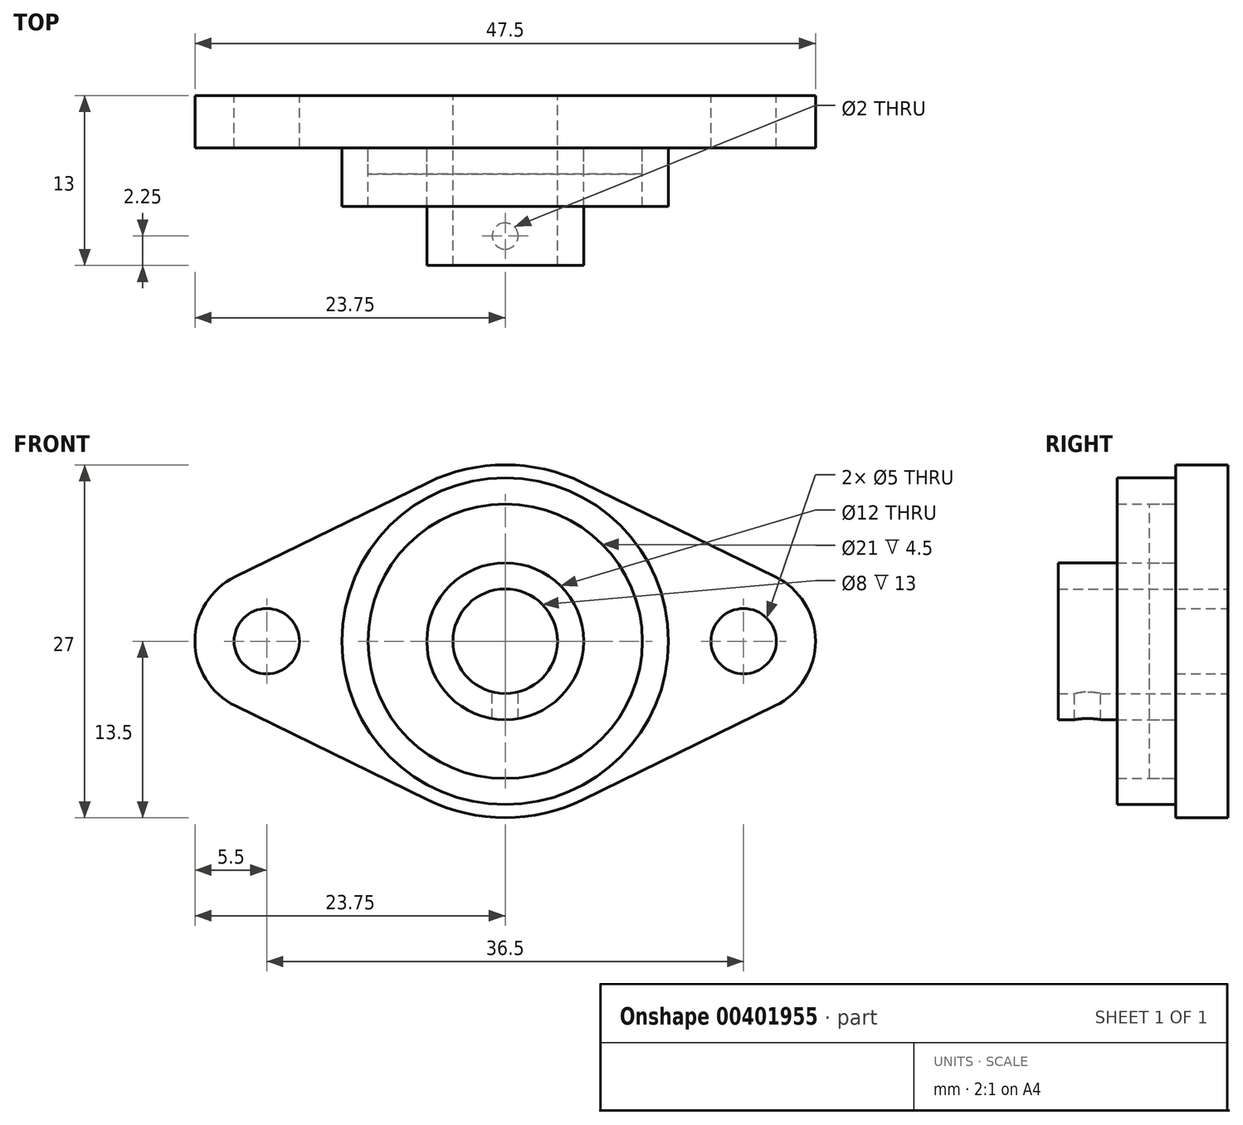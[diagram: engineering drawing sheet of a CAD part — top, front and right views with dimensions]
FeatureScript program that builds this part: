
annotation { "Feature Type Name" : "Feature", "Feature Type Description" : "" }
export const myFeature = defineFeature(function(context is Context, id is Id, definition is map)
    precondition{}
    {
        {
            var Q0;
            Q0=qCreatedBy(makeId("Front.planeOp"),FACE);
            var sketch = newSketch(context, id + "F0", { "sketchPlane" : qUnion([Q0])});
            skArc(sketch, "E0", {"start": v(-20.66, 4.94) * mm, "mid": v(-23.75, 0) * mm, "end": v(-20.66, -4.94) * mm});
            skArc(sketch, "E1", {"start": v(20.66, -4.94) * mm, "mid": v(23.75, 0) * mm, "end": v(20.66, 4.94) * mm});
            skLineSegment(sketch, "E2", {"start": v(-18.25, 0) * mm, "end": v(18.25, 0) * mm, "construction": true});
            skLineSegment(sketch, "E3", {"start": v(-20.66, 4.94) * mm, "end": v(-5.92, 12.13) * mm});
            skLineSegment(sketch, "E4", {"start": v(0, 0) * mm, "end": v(0, 24.56) * mm, "construction": true});
            skLineSegment(sketch, "E5.MirrorCS", {"start": v(20.66, 4.94) * mm, "end": v(5.92, 12.13) * mm});
            skLineSegment(sketch, "E6.MirrorCS", {"start": v(-20.66, -4.94) * mm, "end": v(-5.92, -12.13) * mm});
            skLineSegment(sketch, "E7.MirrorCS", {"start": v(20.66, -4.94) * mm, "end": v(5.92, -12.13) * mm});
            skArc(sketch, "E8.trimOffspring", {"start": v(5.92, 12.13) * mm, "mid": v(0, 13.5) * mm, "end": v(-5.92, 12.13) * mm});
            skArc(sketch, "E9.trimOffspring", {"start": v(-5.92, -12.13) * mm, "mid": v(0, -13.5) * mm, "end": v(5.92, -12.13) * mm});
            skCircle(sketch, "E10", {"center": v(-18.25, 0) * mm, "radius": 2.5 * mm});
            skCircle(sketch, "E11", {"center": v(18.25, 0) * mm, "radius": 2.5 * mm});
            skSolve(sketch);
        }
        {
            var Q0;
            Q0 = qSketchRegion(id + "F0", true);
            extrude(context, id + "F1", {"entities" : qUnion([Q0]), "endBound" : BoundingType.SYMMETRIC, "depth" : 4 * mm});
        }
        {
            var Q0;
            Q0=makeQuery(id+"F1.opExtrude","CAP_FACE",FACE,{"disambiguationData":[OSD([sQuery(id+"F0.wireOp",EDGE,"E0"),sQuery(id+"F0.wireOp",EDGE,"E1"),sQuery(id+"F0.wireOp",EDGE,"E3"),sQuery(id+"F0.wireOp",EDGE,"E5.MirrorCS"),sQuery(id+"F0.wireOp",EDGE,"E6.MirrorCS"),sQuery(id+"F0.wireOp",EDGE,"E7.MirrorCS"),sQuery(id+"F0.wireOp",EDGE,"E8.trimOffspring"),sQuery(id+"F0.wireOp",EDGE,"E9.trimOffspring"),sQuery(id+"F0.wireOp",EDGE,"E10"),sQuery(id+"F0.wireOp",EDGE,"E11")])],"isStart":false});
            var sketch = newSketch(context, id + "F2", { "sketchPlane" : qUnion([Q0])});
            skCircle(sketch, "E12", {"center": v(0, 0) * mm, "radius": 12.5 * mm});
            skCircle(sketch, "E13.0", {"center": v(0, 0) * mm, "radius": 10.5 * mm});
            skSolve(sketch);
        }
        {
            var Q0;
            Q0 = qSketchRegion(id + "F2", true);
            extrude(context, id + "F3", {"entities" : qUnion([Q0]), "operationType" : NewBodyOperationType.ADD, "depth" : 4.5 * mm});
        }
        {
            var Q0;
            Q0=makeQuery(id+"F3.boolean.opBoolean","SPLIT",FACE,{"disambiguationData":[TD([makeQuery(id+"F3.opExtrude","SWEPT_FACE",FACE,{"disambiguationData":[OSD([sQuery(id+"F2.wireOp",EDGE,"E13.0")])]})])],"derivedFrom":makeQuery(id+"F1.opExtrude","CAP_FACE",FACE,{"disambiguationData":[OSD([sQuery(id+"F0.wireOp",EDGE,"E0"),sQuery(id+"F0.wireOp",EDGE,"E1"),sQuery(id+"F0.wireOp",EDGE,"E3"),sQuery(id+"F0.wireOp",EDGE,"E5.MirrorCS"),sQuery(id+"F0.wireOp",EDGE,"E6.MirrorCS"),sQuery(id+"F0.wireOp",EDGE,"E7.MirrorCS"),sQuery(id+"F0.wireOp",EDGE,"E8.trimOffspring"),sQuery(id+"F0.wireOp",EDGE,"E9.trimOffspring"),sQuery(id+"F0.wireOp",EDGE,"E10"),sQuery(id+"F0.wireOp",EDGE,"E11")])],"isStart":false})});
            var sketch = newSketch(context, id + "F4", { "sketchPlane" : qUnion([Q0])});
            skCircle(sketch, "E14", {"center": v(0, 0) * mm, "radius": 4 * mm});
            skCircle(sketch, "E15.0", {"center": v(0, 0) * mm, "radius": 6 * mm});
            skSolve(sketch);
        }
        {
            var Q0;
            Q0 = qSketchRegion(id + "F4", true);
            extrude(context, id + "F5", {"entities" : qUnion([Q0]), "operationType" : NewBodyOperationType.ADD, "depth" : 9 * mm});
        }
        {
            var Q0;
            Q0=makeQuery(id+"F4.imprint","IMPRINT",FACE,{"disambiguationData":[TD([[makeQuery(id+"F4.imprint","IMPRINT",EDGE,{"derivedFrom":sQuery(id+"F4.wireOp",EDGE,"E14")}),1.0]])]});
            extrude(context, id + "F6", {"entities" : qUnion([Q0]), "operationType" : NewBodyOperationType.REMOVE, "endBound" : BoundingType.THROUGH_ALL, "oppositeDirection" : true, "depth" : 25 * mm});
        }
        {
            var Q0;
            {var subQ0=makeQuery(id+"F3.opExtrude","SWEPT_FACE",FACE,{"disambiguationData":[OSD([sQuery(id+"F2.wireOp",EDGE,"E13.0")])]});Q0=makeQuery(id+"F5.boolean.opBoolean","SPLIT",FACE,{"disambiguationData":[TD([subQ0])],"derivedFrom":makeQuery(id+"F3.boolean.opBoolean","SPLIT",FACE,{"disambiguationData":[TD([subQ0])],"derivedFrom":makeQuery(id+"F1.opExtrude","CAP_FACE",FACE,{"disambiguationData":[OSD([sQuery(id+"F0.wireOp",EDGE,"E0"),sQuery(id+"F0.wireOp",EDGE,"E1"),sQuery(id+"F0.wireOp",EDGE,"E3"),sQuery(id+"F0.wireOp",EDGE,"E5.MirrorCS"),sQuery(id+"F0.wireOp",EDGE,"E6.MirrorCS"),sQuery(id+"F0.wireOp",EDGE,"E7.MirrorCS"),sQuery(id+"F0.wireOp",EDGE,"E8.trimOffspring"),sQuery(id+"F0.wireOp",EDGE,"E9.trimOffspring"),sQuery(id+"F0.wireOp",EDGE,"E10"),sQuery(id+"F0.wireOp",EDGE,"E11")])],"isStart":false})})});}
            extrude(context, id + "F7", {"entities" : qUnion([Q0]), "depth" : 2 * mm});
        }
        {
            var Q0;
            Q0=qCreatedBy(makeId("Top.planeOp"),FACE);
            var sketch = newSketch(context, id + "F8", { "sketchPlane" : qUnion([Q0])});
            skLineSegment(sketch, "E16", {"start": v(0, -11) * mm, "end": v(0, -6.5) * mm, "construction": true});
            skCircle(sketch, "E17", {"center": v(0, -8.75) * mm, "radius": 1 * mm});
            skSolve(sketch);
        }
        {
            var Q0;
            Q0 = qSketchRegion(id + "F8", true);
            extrude(context, id + "F9", {"entities" : qUnion([Q0]), "operationType" : NewBodyOperationType.REMOVE, "endBound" : BoundingType.THROUGH_ALL, "oppositeDirection" : true, "depth" : 25 * mm});
        }
    });
